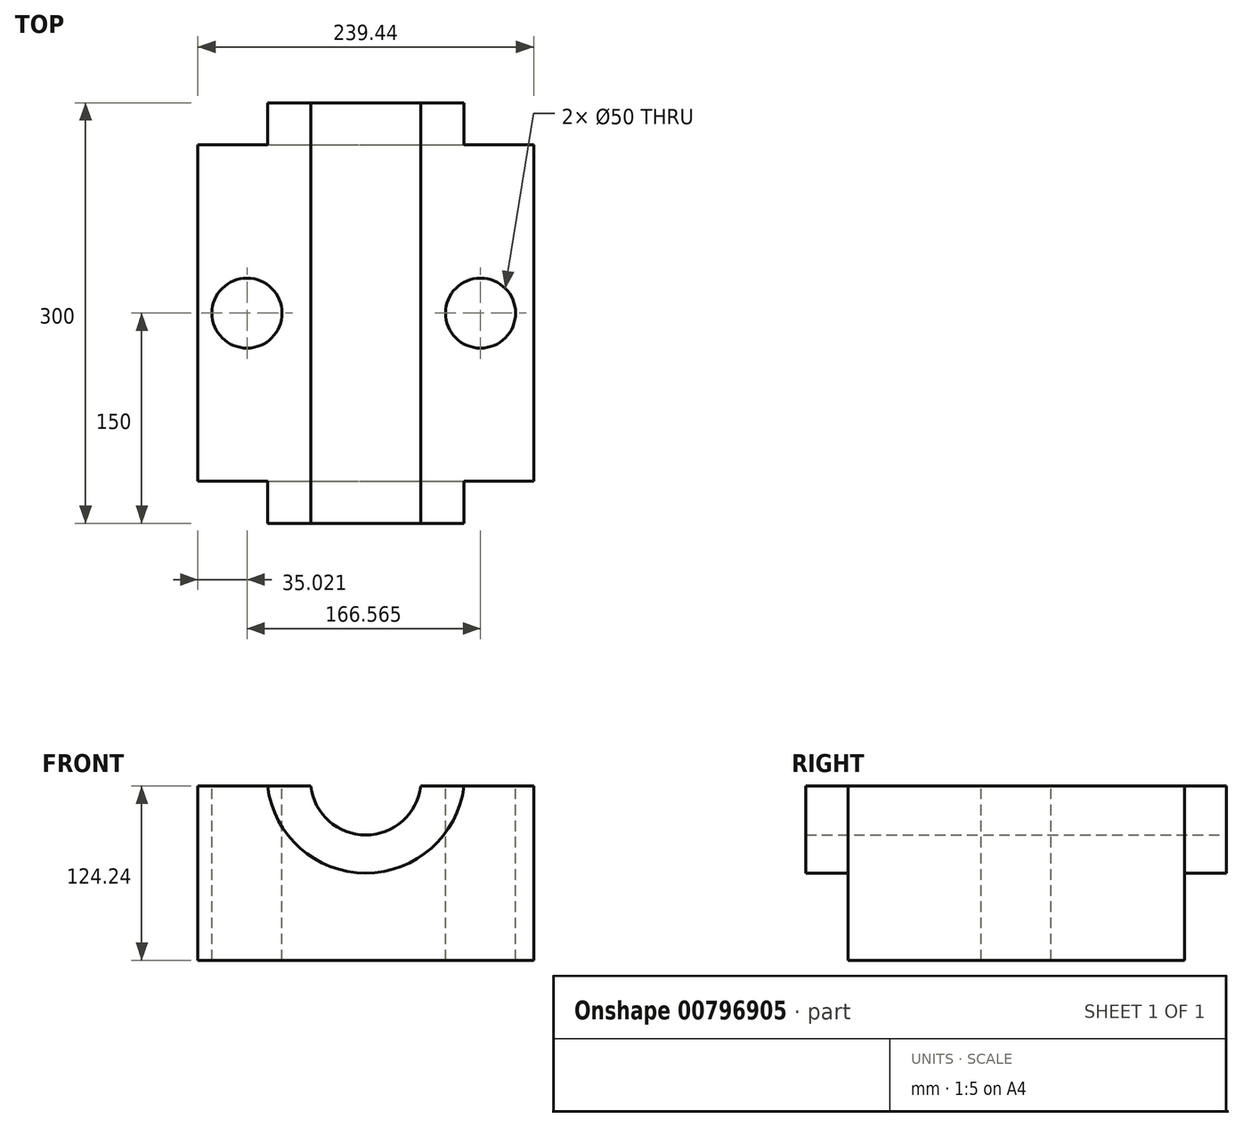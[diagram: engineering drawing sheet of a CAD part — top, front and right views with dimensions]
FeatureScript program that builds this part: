
annotation { "Feature Type Name" : "Feature", "Feature Type Description" : "" }
export const myFeature = defineFeature(function(context is Context, id is Id, definition is map)
    precondition{}
    {
        {
            var Q0;
            Q0=qCreatedBy(makeId("Front.planeOp"),FACE);
            var sketch = newSketch(context, id + "F0", { "sketchPlane" : qUnion([Q0])});
            skLineSegment(sketch, "E0.bottom", {"start": v(-119.72, 62.12) * mm, "end": v(119.72, 62.12) * mm});
            skLineSegment(sketch, "E0.top", {"start": v(-119.72, -62.12) * mm, "end": v(119.72, -62.12) * mm});
            skLineSegment(sketch, "E0.left", {"start": v(-119.72, 62.12) * mm, "end": v(-119.72, -62.12) * mm});
            skLineSegment(sketch, "E0.right", {"start": v(119.72, 62.12) * mm, "end": v(119.72, -62.12) * mm});
            skPoint(sketch, "E0.middle", {"position": v(0, 0) * mm});
            skLineSegment(sketch, "E1.bottom", {"start": v(-70.05, 62.12) * mm, "end": v(70.05, 62.12) * mm});
            skLineSegment(sketch, "E1.top", {"start": v(-70.05, -62.12) * mm, "end": v(70.05, -62.12) * mm});
            skLineSegment(sketch, "E1.left", {"start": v(-70.05, 62.12) * mm, "end": v(-70.05, -62.12) * mm});
            skLineSegment(sketch, "E1.right", {"start": v(70.05, 62.12) * mm, "end": v(70.05, -62.12) * mm});
            skArc(sketch, "E2", {"start": v(-70.05, 62.12) * mm, "mid": v(0, 0.1) * mm, "end": v(70.05, 62.12) * mm});
            skLineSegment(sketch, "E3.bottom", {"start": v(-39.2, 62.12) * mm, "end": v(39.2, 62.12) * mm});
            skLineSegment(sketch, "E3.top", {"start": v(-39.2, 26.87) * mm, "end": v(39.2, 26.87) * mm});
            skLineSegment(sketch, "E3.left", {"start": v(-39.2, 62.12) * mm, "end": v(-39.2, 26.87) * mm});
            skLineSegment(sketch, "E3.right", {"start": v(39.2, 62.12) * mm, "end": v(39.2, 26.87) * mm});
            skPoint(sketch, "E3.middle", {"position": v(0, 44.5) * mm});
            skArc(sketch, "E4", {"start": v(-39.2, 62.12) * mm, "mid": v(0, 27.27) * mm, "end": v(39.2, 62.12) * mm});
            skSolve(sketch);
        }
        {
            var Q0;
            {var subQ0=sQuery(id+"F0.wireOp",EDGE,"E2");Q0=makeQuery(id+"F0.imprint","IMPRINT",FACE,{"disambiguationData":[TD([[makeQuery(id+"F0.imprint","IMPRINT",EDGE,{"derivedFrom":subQ0}),1.0]])]});}
            var Q1;
            Q1=makeQuery(id+"F0.imprint","IMPRINT",FACE,{"disambiguationData":[TD([[makeQuery(id+"F0.imprint","IMPRINT",EDGE,{"derivedFrom":sQuery(id+"F0.wireOp",EDGE,"E3.top")}),1.0]])]});
            extrude(context, id + "F1", {"entities" : qUnion([Q0, Q1]), "depth" : 150 * mm, "offsetDistance" : 25 * mm, "hasSecondDirection" : true, "secondDirectionOppositeDirection" : true, "secondDirectionDepth" : 150 * mm});
        }
        {
            var Q0;
            {var subQ0=sQuery(id+"F0.wireOp",EDGE,"E0.left");Q0=makeQuery(id+"F0.imprint","IMPRINT",FACE,{"disambiguationData":[TD([[makeQuery(id+"F0.imprint","IMPRINT",EDGE,{"derivedFrom":subQ0}),1.0]])]});}
            var Q1;
            {var subQ0=sQuery(id+"F0.wireOp",EDGE,"E1.left");Q1=makeQuery(id+"F0.imprint","IMPRINT",FACE,{"disambiguationData":[TD([[makeQuery(id+"F0.imprint","IMPRINT",EDGE,{"derivedFrom":subQ0}),1.0]])]});}
            var Q2;
            {var subQ0=sQuery(id+"F0.wireOp",EDGE,"E0.right");Q2=makeQuery(id+"F0.imprint","IMPRINT",FACE,{"disambiguationData":[TD([[makeQuery(id+"F0.imprint","IMPRINT",EDGE,{"derivedFrom":subQ0}),-1.0]])]});}
            extrude(context, id + "F2", {"entities" : qUnion([Q0, Q1, Q2]), "operationType" : NewBodyOperationType.ADD, "depth" : 120 * mm, "offsetDistance" : 25 * mm, "hasSecondDirection" : true, "secondDirectionOppositeDirection" : true, "secondDirectionDepth" : 120 * mm});
        }
        {
            var Q0;
            Q0=qCreatedBy(makeId("Top.planeOp"),FACE);
            var sketch = newSketch(context, id + "F3", { "sketchPlane" : qUnion([Q0])});
            skCircle(sketch, "E5", {"center": v(-84.7, 0) * mm, "radius": 30.3 * mm});
            skCircle(sketch, "E6", {"center": v(81.87, 0) * mm, "radius": 31.05 * mm});
            skSolve(sketch);
        }
        {
            var Q0;
            Q0=sQuery(id+"F3.wireOp",VERTEX,"E5.center");
            var Q1;
            Q1=sQuery(id+"F3.wireOp",VERTEX,"E6.center");
            var Q2;
            Q2=makeQuery(id+"F1.opExtrude","SWEPT_BODY",BODY,{"disambiguationData":[OSD([sQuery(id+"F0.wireOp",EDGE,"E0.bottom"),sQuery(id+"F0.wireOp",EDGE,"E2"),sQuery(id+"F0.wireOp",EDGE,"E4")])]});
            hole(context, id + "F4", {"style" : HoleStyle.SIMPLE, "endStyle" : HoleEndStyle.THROUGH, "holeDiameter" : 50 * mm, "majorDiameter" : 5 * mm, "isTappedThrough" : true, "tappedDepth" : 12 * mm, "tapClearance" : 3, "locations" : qUnion([Q0, Q1]), "scope" : qUnion([Q2])});
        }
        {
            var Q0;
            Q0=sQuery(id+"F3.wireOp",VERTEX,"E5.center");
            var Q1;
            Q1=sQuery(id+"F3.wireOp",VERTEX,"E6.center");
            var Q2;
            Q2=makeQuery(id+"F1.opExtrude","SWEPT_BODY",BODY,{"disambiguationData":[OSD([sQuery(id+"F0.wireOp",EDGE,"E1.bottom"),sQuery(id+"F0.wireOp",EDGE,"E2"),sQuery(id+"F0.wireOp",EDGE,"E4")])]});
            hole(context, id + "F5", {"style" : HoleStyle.SIMPLE, "endStyle" : HoleEndStyle.THROUGH, "oppositeDirection" : true, "holeDiameter" : 50 * mm, "majorDiameter" : 5 * mm, "isTappedThrough" : true, "tappedDepth" : 12 * mm, "tapClearance" : 3, "locations" : qUnion([Q0, Q1]), "scope" : qUnion([Q2])});
        }
    });
